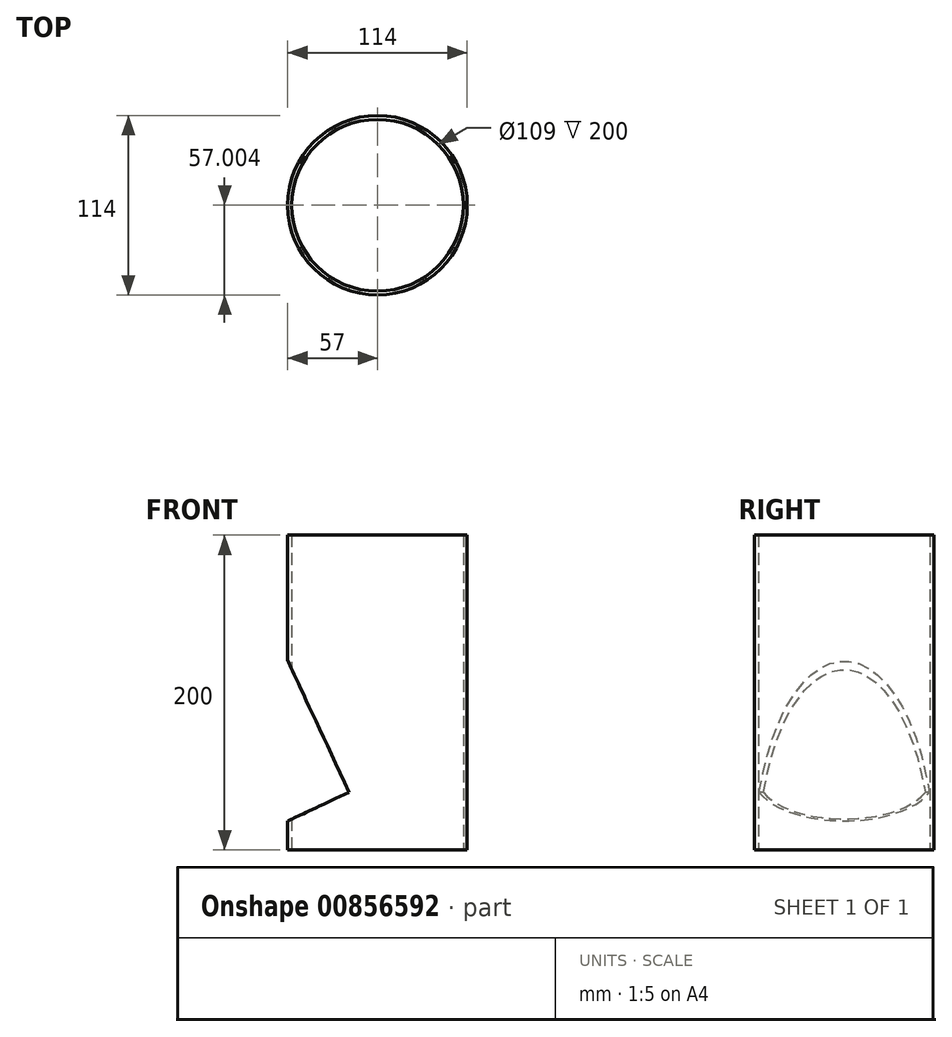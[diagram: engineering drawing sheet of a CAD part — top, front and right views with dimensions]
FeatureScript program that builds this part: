
annotation { "Feature Type Name" : "Feature", "Feature Type Description" : "" }
export const myFeature = defineFeature(function(context is Context, id is Id, definition is map)
    precondition{}
    {
        {
            var Q0;
            Q0=qCreatedBy(makeId("Top.planeOp"),FACE);
            var sketch = newSketch(context, id + "F0", { "sketchPlane" : qUnion([Q0])});
            skCircle(sketch, "E0", {"center": v(0, 3.56) * mm, "radius": 57 * mm});
            skSolve(sketch);
        }
        {
            var Q0;
            Q0 = qSketchRegion(id + "F0", true);
            var Q1;
            Q1=makeQuery(id+"F0.imprint","IMPRINT",FACE,{"disambiguationData":[TD([[makeQuery(id+"F0.imprint","IMPRINT",EDGE,{"derivedFrom":sQuery(id+"F0.wireOp",EDGE,"E0")}),1.0]])]});
            extrude(context, id + "F1", {"entities" : qUnion([Q0, Q1]), "depth" : 200 * mm, "offsetDistance" : 25 * mm});
        }
        {
            var Q0;
            Q0=makeQuery(id+"F1.opExtrude","CAP_FACE",FACE,{"disambiguationData":[OSD([sQuery(id+"F0.wireOp",EDGE,"E0")])],"isStart":true});
            var Q1;
            Q1=makeQuery(id+"F1.opExtrude","CAP_FACE",FACE,{"disambiguationData":[OSD([sQuery(id+"F0.wireOp",EDGE,"E0")])],"isStart":false});
            shell(context, id + "F2", {"entities" : qUnion([Q0, Q1]), "thickness" : 2.5 * mm});
        }
        {
            var Q0;
            Q0=qCreatedBy(makeId("Front.planeOp"),FACE);
            var sketch = newSketch(context, id + "F3", { "sketchPlane" : qUnion([Q0])});
            skLineSegment(sketch, "E1", {"start": v(-57, 18.43) * mm, "end": v(-18, 36.62) * mm});
            skLineSegment(sketch, "E2", {"start": v(-57, 18.43) * mm, "end": v(-57, 120.23) * mm});
            skLineSegment(sketch, "E3", {"start": v(-57, 120.23) * mm, "end": v(-18, 36.62) * mm});
            skSolve(sketch);
        }
        {
            var Q0;
            Q0 = qSketchRegion(id + "F3", true);
            extrude(context, id + "F4", {"entities" : qUnion([Q0]), "operationType" : NewBodyOperationType.REMOVE, "endBound" : BoundingType.SYMMETRIC, "oppositeDirection" : true, "depth" : 120 * mm, "offsetDistance" : 25 * mm});
        }
    });
